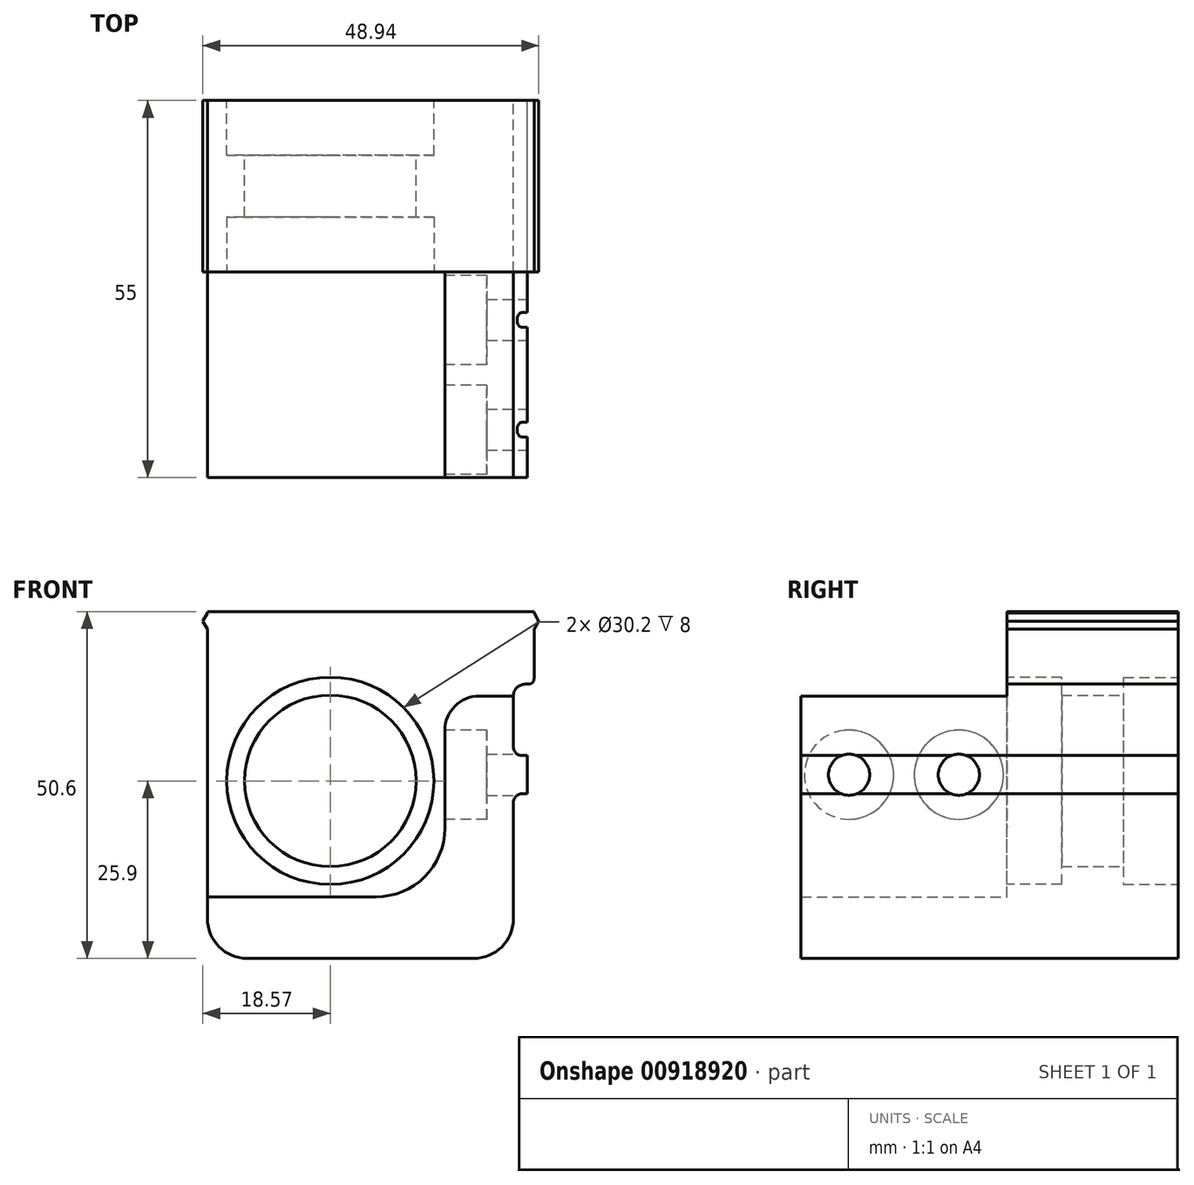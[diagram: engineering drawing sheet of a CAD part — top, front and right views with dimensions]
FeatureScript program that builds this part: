
annotation { "Feature Type Name" : "Feature", "Feature Type Description" : "" }
export const myFeature = defineFeature(function(context is Context, id is Id, definition is map)
    precondition{}
    {
        {
            var Q0;
            Q0=qCreatedBy(makeId("Front.planeOp"),FACE);
            var sketch = newSketch(context, id + "F0", { "sketchPlane" : qUnion([Q0])});
            skLineSegment(sketch, "E0.0", {"start": v(-23.7, 23.56) * mm, "end": v(-23.7, 23.8) * mm});
            skLineSegment(sketch, "E0.1", {"start": v(-24.37, 22.4) * mm, "end": v(-23.7, 23.56) * mm});
            skLineSegment(sketch, "E0.2", {"start": v(-23.7, 21.24) * mm, "end": v(-24.37, 22.4) * mm});
            skLineSegment(sketch, "E0.3", {"start": v(-23.7, -21) * mm, "end": v(-23.7, 21.24) * mm});
            skArc(sketch, "E0.4", {"start": v(-23.7, -21) * mm, "mid": v(-22, -25.1) * mm, "end": v(-17.9, -26.8) * mm});
            skLineSegment(sketch, "E0.5", {"start": v(-23.7, 23.8) * mm, "end": v(23.9, 23.8) * mm});
            skLineSegment(sketch, "E0.6", {"start": v(15.1, -26.8) * mm, "end": v(-17.9, -26.8) * mm});
            skArc(sketch, "E0.7", {"start": v(15.1, -26.8) * mm, "mid": v(19.2, -25.1) * mm, "end": v(20.9, -21) * mm});
            skLineSegment(sketch, "E0.8", {"start": v(20.9, -4) * mm, "end": v(20.9, -21) * mm});
            skArc(sketch, "E0.9", {"start": v(22.1, -2.8) * mm, "mid": v(21.25, -3.15) * mm, "end": v(20.9, -4) * mm});
            skLineSegment(sketch, "E0.10", {"start": v(22.9, -2.8) * mm, "end": v(22.1, -2.8) * mm});
            skLineSegment(sketch, "E0.11", {"start": v(22.9, -2.8) * mm, "end": v(22.9, 2.8) * mm});
            skLineSegment(sketch, "E0.12", {"start": v(23.9, 21.24) * mm, "end": v(23.9, 14) * mm});
            skLineSegment(sketch, "E0.13", {"start": v(24.57, 22.4) * mm, "end": v(23.9, 21.24) * mm});
            skLineSegment(sketch, "E0.14", {"start": v(23.9, 23.56) * mm, "end": v(24.57, 22.4) * mm});
            skLineSegment(sketch, "E0.15", {"start": v(23.9, 23.8) * mm, "end": v(23.9, 23.56) * mm});
            skArc(sketch, "E0.16", {"start": v(23.1, 13.2) * mm, "mid": v(23.67, 13.43) * mm, "end": v(23.9, 14) * mm});
            skLineSegment(sketch, "E0.17", {"start": v(23.1, 13.2) * mm, "end": v(22.6, 13.2) * mm});
            skArc(sketch, "E0.18", {"start": v(22.6, 13.2) * mm, "mid": v(21.4, 12.7) * mm, "end": v(20.9, 11.5) * mm});
            skLineSegment(sketch, "E0.19", {"start": v(20.9, 11.5) * mm, "end": v(20.9, 4) * mm});
            skArc(sketch, "E0.20", {"start": v(20.9, 4) * mm, "mid": v(21.25, 3.15) * mm, "end": v(22.1, 2.8) * mm});
            skLineSegment(sketch, "E0.21", {"start": v(22.1, 2.8) * mm, "end": v(22.9, 2.8) * mm});
            skSolve(sketch);
        }
        {
            var Q0;
            Q0 = qSketchRegion(id + "F0", true);
            extrude(context, id + "F1", {"entities" : qUnion([Q0]), "depth" : 55 * mm, "offsetDistance" : 25 * mm});
        }
        {
            var Q0;
            Q0=makeQuery(id+"F1.opExtrude","CAP_FACE",FACE,{"disambiguationData":[OSD([sQuery(id+"F0.wireOp",EDGE,"E0.0"),sQuery(id+"F0.wireOp",EDGE,"E0.1"),sQuery(id+"F0.wireOp",EDGE,"E0.2"),sQuery(id+"F0.wireOp",EDGE,"E0.3"),sQuery(id+"F0.wireOp",EDGE,"E0.4"),sQuery(id+"F0.wireOp",EDGE,"E0.5"),sQuery(id+"F0.wireOp",EDGE,"E0.6"),sQuery(id+"F0.wireOp",EDGE,"E0.7"),sQuery(id+"F0.wireOp",EDGE,"E0.8"),sQuery(id+"F0.wireOp",EDGE,"E0.9"),sQuery(id+"F0.wireOp",EDGE,"E0.10"),sQuery(id+"F0.wireOp",EDGE,"E0.11"),sQuery(id+"F0.wireOp",EDGE,"E0.12"),sQuery(id+"F0.wireOp",EDGE,"E0.13"),sQuery(id+"F0.wireOp",EDGE,"E0.14"),sQuery(id+"F0.wireOp",EDGE,"E0.15"),sQuery(id+"F0.wireOp",EDGE,"E0.16"),sQuery(id+"F0.wireOp",EDGE,"E0.17"),sQuery(id+"F0.wireOp",EDGE,"E0.18"),sQuery(id+"F0.wireOp",EDGE,"E0.19"),sQuery(id+"F0.wireOp",EDGE,"E0.20"),sQuery(id+"F0.wireOp",EDGE,"E0.21")])],"isStart":false});
            var sketch = newSketch(context, id + "F2", { "sketchPlane" : qUnion([Q0])});
            skLineSegment(sketch, "E1", {"start": v(26.68, 11.46) * mm, "end": v(15.9, 11.46) * mm});
            skLineSegment(sketch, "E2", {"start": v(10.9, 6.46) * mm, "end": v(10.9, -11.8) * mm});
            skLineSegment(sketch, "E3", {"start": v(5.9, -17.8) * mm, "end": v(-26.83, -17.8) * mm});
            skLineSegment(sketch, "E4", {"start": v(-26.83, -17.8) * mm, "end": v(-26.83, 26.7) * mm});
            skLineSegment(sketch, "E5", {"start": v(-26.83, 26.7) * mm, "end": v(26.68, 26.7) * mm});
            skLineSegment(sketch, "E6", {"start": v(26.68, 26.7) * mm, "end": v(26.68, 11.46) * mm});
            skPoint(sketch, "E7.visualSharp", {"position": v(10.9, -17.8) * mm});
            skPoint(sketch, "E8.visualSharp", {"position": v(10.9, 11.46) * mm});
            skArc(sketch, "E8.filletArc", {"start": v(15.9, 11.46) * mm, "mid": v(12.36, 10) * mm, "end": v(10.9, 6.46) * mm});
            skLineSegment(sketch, "E9", {"start": v(5.9, -17.8) * mm, "end": v(10.9, -17.8) * mm});
            skLineSegment(sketch, "E10", {"start": v(10.9, -11.8) * mm, "end": v(10.9, -17.8) * mm});
            skSolve(sketch);
        }
        {
            var Q0;
            Q0 = qSketchRegion(id + "F2", true);
            extrude(context, id + "F3", {"entities" : qUnion([Q0]), "operationType" : NewBodyOperationType.REMOVE, "oppositeDirection" : true, "depth" : 30 * mm, "offsetDistance" : 25 * mm});
        }
        {
            var Q0;
            Q0=makeQuery(id+"F1.opExtrude","SWEPT_FACE",FACE,{"disambiguationData":[OSD([sQuery(id+"F0.wireOp",EDGE,"E0.11")])]});
            var sketch = newSketch(context, id + "F4", { "sketchPlane" : qUnion([Q0])});
            skCircle(sketch, "E11", {"center": v(-48, 0) * mm, "radius": 3 * mm});
            skCircle(sketch, "E12", {"center": v(-32, 0) * mm, "radius": 3 * mm});
            skSolve(sketch);
        }
        {
            var Q0;
            Q0 = qSketchRegion(id + "F4", true);
            extrude(context, id + "F5", {"entities" : qUnion([Q0]), "operationType" : NewBodyOperationType.REMOVE, "oppositeDirection" : true, "depth" : 25 * mm, "offsetDistance" : 25 * mm});
        }
        {
            var Q0;
            Q0=makeQuery(id+"F1.opExtrude","CAP_FACE",FACE,{"disambiguationData":[OSD([sQuery(id+"F0.wireOp",EDGE,"E0.0"),sQuery(id+"F0.wireOp",EDGE,"E0.1"),sQuery(id+"F0.wireOp",EDGE,"E0.2"),sQuery(id+"F0.wireOp",EDGE,"E0.3"),sQuery(id+"F0.wireOp",EDGE,"E0.4"),sQuery(id+"F0.wireOp",EDGE,"E0.5"),sQuery(id+"F0.wireOp",EDGE,"E0.6"),sQuery(id+"F0.wireOp",EDGE,"E0.7"),sQuery(id+"F0.wireOp",EDGE,"E0.8"),sQuery(id+"F0.wireOp",EDGE,"E0.9"),sQuery(id+"F0.wireOp",EDGE,"E0.10"),sQuery(id+"F0.wireOp",EDGE,"E0.11"),sQuery(id+"F0.wireOp",EDGE,"E0.12"),sQuery(id+"F0.wireOp",EDGE,"E0.13"),sQuery(id+"F0.wireOp",EDGE,"E0.14"),sQuery(id+"F0.wireOp",EDGE,"E0.15"),sQuery(id+"F0.wireOp",EDGE,"E0.16"),sQuery(id+"F0.wireOp",EDGE,"E0.17"),sQuery(id+"F0.wireOp",EDGE,"E0.18"),sQuery(id+"F0.wireOp",EDGE,"E0.19"),sQuery(id+"F0.wireOp",EDGE,"E0.20"),sQuery(id+"F0.wireOp",EDGE,"E0.21")])],"isStart":true});
            var sketch = newSketch(context, id + "F6", { "sketchPlane" : qUnion([Q0])});
            skCircle(sketch, "E13", {"center": v(5.8, -0.9) * mm, "radius": 12.5 * mm});
            skLineSegment(sketch, "E14.bottom", {"start": v(-10.7, 22.1) * mm, "end": v(22.3, 22.1) * mm, "construction": true});
            skLineSegment(sketch, "E14.top", {"start": v(-10.7, -23.9) * mm, "end": v(22.3, -23.9) * mm, "construction": true});
            skLineSegment(sketch, "E14.left", {"start": v(-10.7, 22.1) * mm, "end": v(-10.7, -23.9) * mm, "construction": true});
            skLineSegment(sketch, "E14.right", {"start": v(22.3, 22.1) * mm, "end": v(22.3, -23.9) * mm, "construction": true});
            skSolve(sketch);
        }
        {
            var Q0;
            Q0 = qSketchRegion(id + "F6", true);
            extrude(context, id + "F7", {"entities" : qUnion([Q0]), "operationType" : NewBodyOperationType.REMOVE, "endBound" : BoundingType.UP_TO_NEXT, "oppositeDirection" : true, "depth" : 25 * mm, "offsetDistance" : 25 * mm});
        }
        {
            var Q0;
            Q0=makeQuery(id+"F1.opExtrude","CAP_FACE",FACE,{"disambiguationData":[OSD([sQuery(id+"F0.wireOp",EDGE,"E0.0"),sQuery(id+"F0.wireOp",EDGE,"E0.1"),sQuery(id+"F0.wireOp",EDGE,"E0.2"),sQuery(id+"F0.wireOp",EDGE,"E0.3"),sQuery(id+"F0.wireOp",EDGE,"E0.4"),sQuery(id+"F0.wireOp",EDGE,"E0.5"),sQuery(id+"F0.wireOp",EDGE,"E0.6"),sQuery(id+"F0.wireOp",EDGE,"E0.7"),sQuery(id+"F0.wireOp",EDGE,"E0.8"),sQuery(id+"F0.wireOp",EDGE,"E0.9"),sQuery(id+"F0.wireOp",EDGE,"E0.10"),sQuery(id+"F0.wireOp",EDGE,"E0.11"),sQuery(id+"F0.wireOp",EDGE,"E0.12"),sQuery(id+"F0.wireOp",EDGE,"E0.13"),sQuery(id+"F0.wireOp",EDGE,"E0.14"),sQuery(id+"F0.wireOp",EDGE,"E0.15"),sQuery(id+"F0.wireOp",EDGE,"E0.16"),sQuery(id+"F0.wireOp",EDGE,"E0.17"),sQuery(id+"F0.wireOp",EDGE,"E0.18"),sQuery(id+"F0.wireOp",EDGE,"E0.19"),sQuery(id+"F0.wireOp",EDGE,"E0.20"),sQuery(id+"F0.wireOp",EDGE,"E0.21")])],"isStart":false});
            var sketch = newSketch(context, id + "F8", { "sketchPlane" : qUnion([Q0])});
            skCircle(sketch, "E15", {"center": v(-5.8, -0.9) * mm, "radius": 15.1 * mm});
            skSolve(sketch);
        }
        {
            var Q0;
            Q0 = qSketchRegion(id + "F8", true);
            extrude(context, id + "F9", {"entities" : qUnion([Q0]), "operationType" : NewBodyOperationType.REMOVE, "oppositeDirection" : true, "depth" : 38 * mm, "offsetDistance" : 25 * mm});
        }
        {
            var Q0;
            Q0=makeQuery(id+"F1.opExtrude","CAP_FACE",FACE,{"disambiguationData":[OSD([sQuery(id+"F0.wireOp",EDGE,"E0.0"),sQuery(id+"F0.wireOp",EDGE,"E0.1"),sQuery(id+"F0.wireOp",EDGE,"E0.2"),sQuery(id+"F0.wireOp",EDGE,"E0.3"),sQuery(id+"F0.wireOp",EDGE,"E0.4"),sQuery(id+"F0.wireOp",EDGE,"E0.5"),sQuery(id+"F0.wireOp",EDGE,"E0.6"),sQuery(id+"F0.wireOp",EDGE,"E0.7"),sQuery(id+"F0.wireOp",EDGE,"E0.8"),sQuery(id+"F0.wireOp",EDGE,"E0.9"),sQuery(id+"F0.wireOp",EDGE,"E0.10"),sQuery(id+"F0.wireOp",EDGE,"E0.11"),sQuery(id+"F0.wireOp",EDGE,"E0.12"),sQuery(id+"F0.wireOp",EDGE,"E0.13"),sQuery(id+"F0.wireOp",EDGE,"E0.14"),sQuery(id+"F0.wireOp",EDGE,"E0.15"),sQuery(id+"F0.wireOp",EDGE,"E0.16"),sQuery(id+"F0.wireOp",EDGE,"E0.17"),sQuery(id+"F0.wireOp",EDGE,"E0.18"),sQuery(id+"F0.wireOp",EDGE,"E0.19"),sQuery(id+"F0.wireOp",EDGE,"E0.20"),sQuery(id+"F0.wireOp",EDGE,"E0.21")])],"isStart":true});
            var sketch = newSketch(context, id + "F10", { "sketchPlane" : qUnion([Q0])});
            skCircle(sketch, "E16", {"center": v(5.8, -0.9) * mm, "radius": 15.1 * mm});
            skSolve(sketch);
        }
        {
            var Q0;
            Q0 = qSketchRegion(id + "F10", true);
            extrude(context, id + "F11", {"entities" : qUnion([Q0]), "operationType" : NewBodyOperationType.REMOVE, "oppositeDirection" : true, "depth" : 8 * mm, "offsetDistance" : 25 * mm});
        }
        {
            var Q0;
            Q0=qCreatedBy(makeId("Right.planeOp"),FACE);
            var sketch = newSketch(context, id + "F12", { "sketchPlane" : qUnion([Q0])});
            skCircle(sketch, "E17", {"center": v(-32, 0) * mm, "radius": 6.5 * mm});
            skCircle(sketch, "E18", {"center": v(-48, 0) * mm, "radius": 6.5 * mm});
            skSolve(sketch);
        }
        {
            var Q0;
            Q0 = qSketchRegion(id + "F12", true);
            extrude(context, id + "F13", {"entities" : qUnion([Q0]), "operationType" : NewBodyOperationType.REMOVE, "depth" : 17 * mm, "offsetDistance" : 25 * mm});
        }
        {
            var Q0;
            Q0=makeQuery(id+"F3.boolean.opBoolean","COPY",EDGE,{"derivedFrom":makeQuery(id+"F3.opExtrude","SWEPT_EDGE",EDGE,{"disambiguationData":[OSD([sQuery(id+"F2.wireOp",EDGE,"E9"),sQuery(id+"F2.wireOp",EDGE,"E10")])]})});
            fillet(context, id + "F14", {"entities" : qUnion([Q0]), "radius" : 10 * mm, "tangentPropagation" : true, "allowEdgeOverflow" : false});
        }
    });
